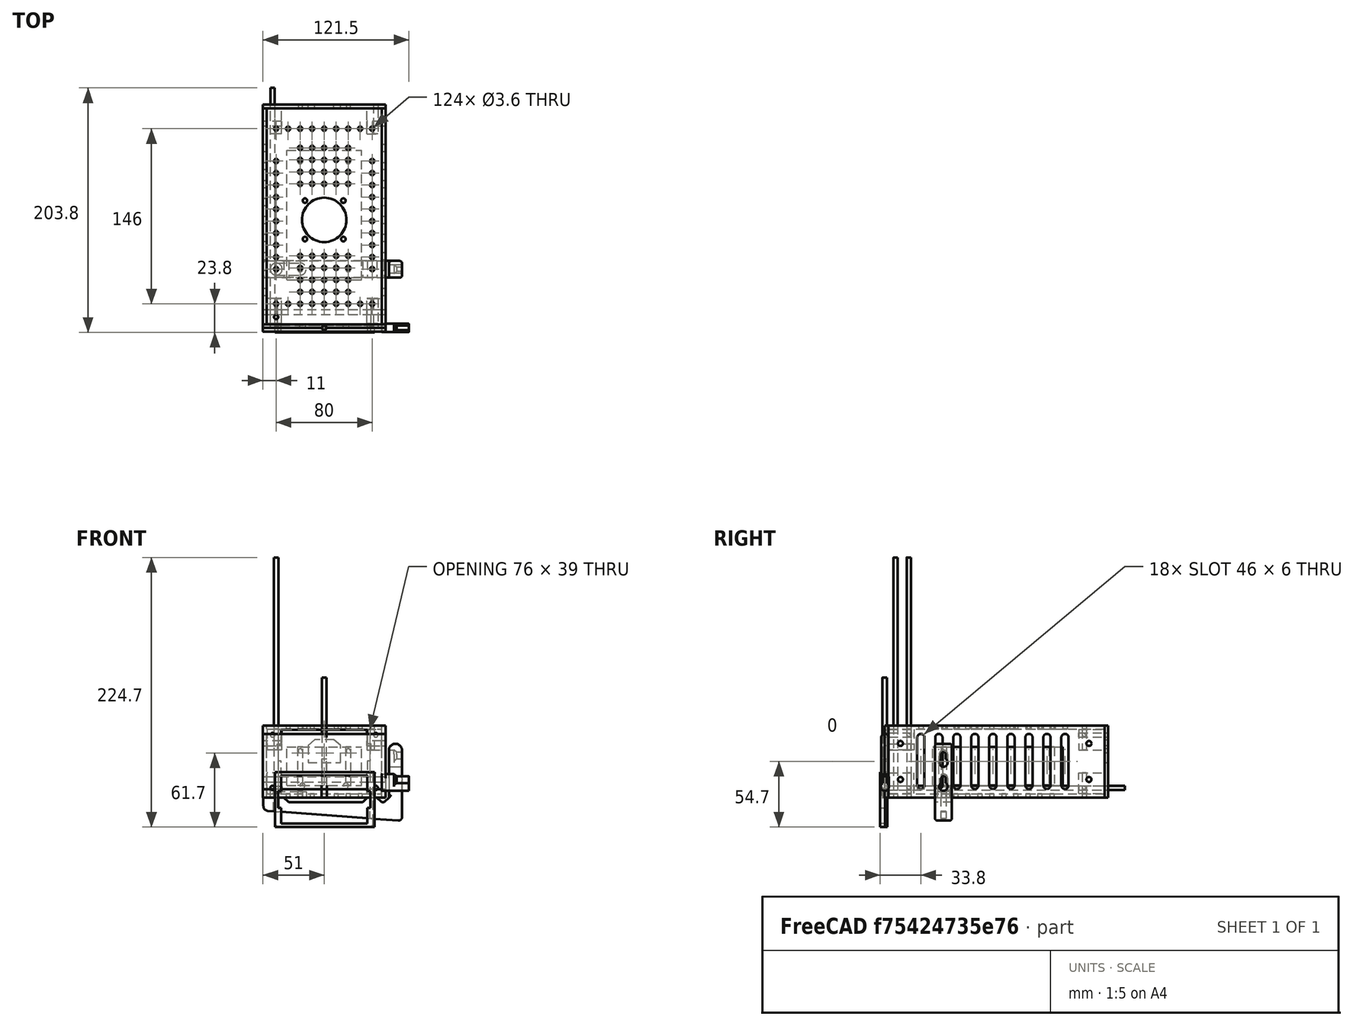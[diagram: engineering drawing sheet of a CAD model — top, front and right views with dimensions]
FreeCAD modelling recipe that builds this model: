
FCSTD DOCUMENT  (FreeCAD 0.21R33694 (Git))
Label: XY-SK35
License: All rights reserved
LicenseURL: http://en.wikipedia.org/wiki/All_rights_reserved
objects: Part::MultiFuse×13, Part::Box×12, Part::Cylinder×12, Part::Cut×10, Sketcher::SketchObject×9, Part::FeaturePython×9, Part::Extrusion×8, Part::Compound×3, Part::Mirroring×3, Part::Feature×1, Part::MultiCommon×1, Spreadsheet::Sheet×1, Part::Part2DObjectPython×1, Part::Fillet×1, Part::Loft×1
note: 75 computed .brp shape members not serialized (recipe doc carries the construction recipe); baked Part::Feature solids carry a one-line shape summary decoded from their .brp

FEATURE [Part::Box] Box  label="Cube"
  AttacherType = Attacher::AttachEngine3D
  Height = 32
  Length = 83
  Placement = pos=(8,29,0) rot=(0,0,1;0rad)
  Width = 46
FEATURE [Part::Feature] front_panel001001001_solid  label="front_panel001001001 (Solid)"
  shape: bbox 102 x 85 x 6 mm, 8704 faces (baked)
FEATURE [Part::MultiCommon] Common
  Placement = pos=(-49,-3.8,50.3) rot=(-1,0,0;1.5708rad)
  Shapes = -> [Box,front_panel001001001_solid]
FEATURE [Part::Box] Box001  label="display cube"
  AttacherType = Attacher::AttachEngine3D
  Height = 60
  Length = 102
  Placement = pos=(-51,0,0) rot=(0,0,1;0rad)
  Width = 3
  expr: .Placement.Base.x = -Length / 2
FEATURE [Part::Cylinder] Cylinder  label="hole_plus"
  Angle = 360
  AttacherType = Attacher::AttachEngine3D
  FirstAngle = 0
  Height = 10
  Placement = pos=(-18.1,10,10) rot=(1,0,0;1.5708rad)
  Radius = 2.1
  SecondAngle = 0
  expr: .Placement.Base.y = Height
FEATURE [Sketcher::SketchObject] Sketch  label="display hole sketch"
  FullyConstrained = true
  Placement = pos=(0,0,0) rot=(1,0,0;1.5708rad)
  sketch-geometry (12):
    g0: LineSegment StartX=-36 StartY=19.5 StartZ=0 EndX=36 EndY=19.5 EndZ=0
    g1: LineSegment StartX=36 StartY=19.5 StartZ=0 EndX=36 EndY=6.5 EndZ=0
    g2: LineSegment StartX=36 StartY=6.5 StartZ=0 EndX=38 EndY=6.5 EndZ=0
    g3: LineSegment StartX=38 StartY=6.5 StartZ=0 EndX=38 EndY=-6.5 EndZ=0
    g4: LineSegment StartX=38 StartY=-6.5 StartZ=0 EndX=36 EndY=-6.5 EndZ=0
    g5: LineSegment StartX=36 StartY=-6.5 StartZ=0 EndX=36 EndY=-19.5 EndZ=0
    g6: LineSegment StartX=36 StartY=-19.5 StartZ=0 EndX=-36 EndY=-19.5 EndZ=0
    g7: LineSegment StartX=-36 StartY=-19.5 StartZ=0 EndX=-36 EndY=-6.5 EndZ=0
    g8: LineSegment StartX=-36 StartY=-6.5 StartZ=0 EndX=-38 EndY=-6.5 EndZ=0
    g9: LineSegment StartX=-38 StartY=-6.5 StartZ=0 EndX=-38 EndY=6.5 EndZ=0
    g10: LineSegment StartX=-38 StartY=6.5 StartZ=0 EndX=-36 EndY=6.5 EndZ=0
    g11: LineSegment StartX=-36 StartY=6.5 StartZ=0 EndX=-36 EndY=19.5 EndZ=0
  constraints (36):
    c: Vertical(g1)
    c: Coincident(g2,g1)
    c: Horizontal(g2)
    c: Coincident(g3,g2)
    c: Coincident(g4,g3)
    c: Coincident(g5,g4)
    c: Vertical(g5)
    c: Coincident(g6,g5)
    c: Horizontal(g6)
    c: Coincident(g7,g6)
    c: Vertical(g7)
    c: Coincident(g8,g7)
    c: Coincident(g9,g8)
    c: Vertical(g9)
    c: Coincident(g10,g9)
    c: Horizontal(g10)
    c: Coincident(g11,g0)
    c: Vertical(g11)
    c: Equal(g0,g6)
    c: Equal(g7,g5)
    c: Equal(g3,g9)
    c: Equal(g10,g8)
    c: Equal(g8,g4)
    c: DistanceX(g0,g0) = 72
    c: DistanceY(g9,g9) = 13  'display_tab_height'
    c: Coincident(g11,g10)
    c: DistanceX(g10,g10) = 2
    c: Symmetric(g1,g10,g-2)
    c: Symmetric(g5,g0,g-1)
    c: Symmetric(g2,g3,g-1)
    c: DistanceY(g7,g7) = 13
    c: Coincident(g1,g0)
    c: Horizontal(g0)
    c: DistanceY(g5,g0) = 39  'display_hole_max_height'
    c: DistanceX(g9,g2) = 76  'display_hole_max_size'
    c: DistanceY(g5,g1) = 26  'bottom_to_tab_top'
FEATURE [Part::Extrusion] Extrude  label="display hole extrude"
  Base = -> Sketch
  Dir = (0,-1,2e-16)
  DirMode = 2
  FaceMakerClass = Part::FaceMakerBullseye
  LengthFwd = 10
  LengthRev = 0
  Placement = pos=(0,0,37) rot=(0,0,1;0rad)
  Reversed = true
  Solid = true
  Symmetric = false
FEATURE [Part::Cylinder] Cylinder001  label="hole_minus"
  Angle = 360
  AttacherType = Attacher::AttachEngine3D
  FirstAngle = 0
  Height = 10
  Placement = pos=(18.1,10,10) rot=(1,0,0;1.5708rad)
  Radius = 2.1
  SecondAngle = 0
  expr: .Placement.Base.x = -<<hole_plus>>.Placement.Base.x
  expr: .Placement.Base.y = <<hole_plus>>.Placement.Base.y
  expr: .Placement.Base.z = <<hole_plus>>.Placement.Base.z
  expr: Radius = <<hole_plus>>.Radius
FEATURE [Part::Cylinder] Cylinder002  label="bolt hole"
  Angle = 360
  AttacherType = Attacher::AttachEngine3D
  FirstAngle = 0
  Height = 200
  Placement = pos=(-43,200,8) rot=(1,0,0;1.5708rad)
  Radius = 1.8
  SecondAngle = 0
  expr: .Placement.Base.x = -<<display cube>>.Length / 2 + <<p>>.bolt2wall
  expr: .Placement.Base.y = Height
  expr: .Placement.Base.z = <<p>>.bolt2wall
  expr: Radius = <<p>>.bolt_hole_radius
FEATURE [Part::FeaturePython] Array  label="bolt hole array"  # Draft array (typed FeaturePython)
  AlwaysSyncPlacement = false
  Angle = 360
  ArrayType = 0
  Axis = (0,0,1)
  Base = -> Cylinder002
  Center = (0,0,0)
  Count = 4
  ExpandArray = false
  Fuse = false
  IntervalAxis = (0,0,0)
  IntervalX = (86,0,0)
  IntervalY = (0,100,0)
  IntervalZ = (0,0,44)
  NumberCircles = 3
  NumberPolar = 5
  NumberX = 2
  NumberY = 1
  NumberZ = 2
  PlacementList = 4 placements: [(-43,200,8),(-43,200,52),(43,200,8),(43,200,52)]
  RadialDistance = 50
  ScaleList = (4) [(1,1,1),(1,1,1),(1,1,1),(1,1,1)]
  Symmetry = 1
  TangentialDistance = 25
  expr: .IntervalX.x = <<display cube>>.Length - 2 * <<p>>.bolt2wall
  expr: .IntervalZ.z = <<display cube>>.Height - 2 * <<p>>.bolt2wall
FEATURE [Part::MultiFuse] Fusion  label="hole fusion"
  Shapes = -> [Array,Cylinder001,Cylinder,Extrude]
FEATURE [Part::Cut] Cut  label="front panel cut"
  Base = -> Box001
  Tool = -> Fusion
FEATURE [Spreadsheet::Sheet] Spreadsheet  label="p"
  cells = A1='bolt2wall; B1(bolt2wall)==8 mm; A2='plate_wall; B2(plate_wall)==3 mm; A3='bolt_hole_radius; B3(bolt_hole_radius)==1.8 mm; A4='fan_bolt_hole; B4(fan_bolt_hole)==2.2 mm; A5='fan_hole_radius; B5(fan_hole_radius)==18.5 mm; A6='screw_top_radius; B6(screw_top_radius)==3.5 mm; A7='screw_radius; B7(screw_radius)==1.8 mm
FEATURE [Part::Box] Box002  label="psu bottom cube"
  AttacherType = Attacher::AttachEngine3D
  Height = 3
  Length = 96
  Placement = pos=(-48,3,0) rot=(0,0,1;0rad)
  Width = 180
  expr: .Placement.Base.x = -Length / 2
  expr: .Placement.Base.y = <<p>>.plate_wall
  expr: Height = <<p>>.plate_wall
  expr: Length = <<display cube>>.Length - 2 * <<p>>.plate_wall
FEATURE [Part::Box] Box003  label="psu side cube"
  AttacherType = Attacher::AttachEngine3D
  Height = 60
  Length = 3
  Placement = pos=(-51,3,0) rot=(0,0,1;0rad)
  Width = 180
  expr: .Placement.Base.x = -<<display cube>>.Length / 2
  expr: .Placement.Base.y = <<p>>.plate_wall
  expr: Height = <<display cube>>.Height
  expr: Length = <<p>>.plate_wall
  expr: Width = <<psu bottom cube>>.Width
FEATURE [Part::Box] Box004  label="psu side cube001"
  AttacherType = Attacher::AttachEngine3D
  Height = 60
  Length = 3
  Placement = pos=(48,3,0) rot=(0,0,1;0rad)
  Width = 180
  expr: .Placement.Base.x = <<display cube>>.Length / 2 - <<p>>.plate_wall
  expr: .Placement.Base.y = <<p>>.plate_wall
  expr: Height = <<display cube>>.Height
  expr: Length = <<p>>.plate_wall
  expr: Width = <<psu bottom cube>>.Width
FEATURE [Part::Cylinder] Cylinder003  label="bolt side hole"
  Angle = 360
  AttacherType = Attacher::AttachEngine3D
  FirstAngle = 0
  Height = 102
  Placement = pos=(-51,13,15) rot=(0,1,0;1.5708rad)
  Radius = 2.1
  SecondAngle = 0
  expr: .Placement.Base.x = -<<display cube>>.Length / 2
  expr: .Placement.Base.y = <<p>>.plate_wall + 10 mm
  expr: Height = <<display cube>>.Length
FEATURE [Part::FeaturePython] Array001  label="bolt side hole array"  # Draft array (typed FeaturePython)
  AlwaysSyncPlacement = false
  Angle = 360
  ArrayType = 0
  Axis = (0,0,1)
  Base = -> Cylinder003
  Center = (0,0,0)
  Count = 4
  ExpandArray = false
  Fuse = false
  IntervalAxis = (0,0,0)
  IntervalX = (100,0,0)
  IntervalY = (0,157,0)
  IntervalZ = (0,0,30)
  NumberCircles = 3
  NumberPolar = 5
  NumberX = 1
  NumberY = 2
  NumberZ = 2
  PlacementList = 4 placements: [(-51,13,15),(-51,13,45),(-51,170,15),(-51,170,45)]
  RadialDistance = 50
  ScaleList = (4) [(1,1,1),(1,1,1),(1,1,1),(1,1,1)]
  Symmetry = 1
  TangentialDistance = 25
  expr: .IntervalY.y = <<psu bottom cube>>.Width - 2 * <<bolt side hole>>.Placement.Base.y + <<p>>.plate_wall
  expr: .IntervalZ.z = <<display cube>>.Height - 2 * <<bolt side hole>>.Placement.Base.z
FEATURE [Sketcher::SketchObject] Sketch001  label="side vent sketch"
  FullyConstrained = true
  Placement = pos=(0,0,0) rot=(0.57735,0.57735,0.57735;2.0944rad)
  expr: Constraints[9] = (<<psu side cube>>.Height - .Constraints.vent_hole_height) / 2
  sketch-geometry (4):
    g0: LineSegment StartX=-3 StartY=50 StartZ=0 EndX=-3 EndY=10 EndZ=0
    g1: LineSegment StartX=3 StartY=50 StartZ=0 EndX=3 EndY=10 EndZ=0
    g2: ArcOfCircle CenterX=0 CenterY=50 CenterZ=0 NormalX=0 NormalY=0 NormalZ=1 AngleXU=0 Radius=3 StartAngle=3e-16 EndAngle=3.14159
    g3: ArcOfCircle CenterX=1e-16 CenterY=10 CenterZ=0 NormalX=0 NormalY=0 NormalZ=1 AngleXU=0 Radius=3 StartAngle=3.14159 EndAngle=6.28319
  constraints (11):
    c: Vertical(g1)
    c: Vertical(g0)
    c: Coincident(g3,g1)
    c: Equal(g1,g0)
    c: Tangent(g2,g0) = -1.5708
    c: Tangent(g2,g1) = 1.5708
    c: Tangent(g3,g0) = -1.5708
    c: Radius(g3) = 3
    c: DistanceY(g0,g0) = 40  'vent_hole_height'
    c: DistanceY(g-1,g0) = 10
    c: PointOnObject(g2,g-2)
FEATURE [Part::Extrusion] Extrude001  label="side vent extrude"
  Base = -> Sketch001
  Dir = (1,0,0)
  DirMode = 2
  FaceMakerClass = Part::FaceMakerBullseye
  LengthFwd = 102
  LengthRev = 0
  Solid = true
  Symmetric = true
  expr: LengthFwd = <<display cube>>.Length
FEATURE [Part::FeaturePython] Array002  label="side vent array"  # Draft array (typed FeaturePython)
  AlwaysSyncPlacement = false
  Angle = 360
  ArrayType = 0
  Axis = (0,0,1)
  Base = -> Extrude001
  Center = (0,0,0)
  Count = 9
  ExpandArray = false
  Fuse = false
  IntervalAxis = (0,0,0)
  IntervalX = (100,0,0)
  IntervalY = (0,15,0)
  IntervalZ = (0,0,100)
  NumberCircles = 3
  NumberPolar = 5
  NumberX = 1
  NumberY = 9
  NumberZ = 1
  Placement = pos=(0,30,0) rot=(0,0,1;0rad)
  PlacementList = 9 placements: arithmetic series from (0,0,0) step (0,15,0) to (0,120,0)
  RadialDistance = 50
  ScaleList = (9) [(1,1,1),(1,1,1),(1,1,1),(1,1,1),(1,1,1),(1,1,1),(1,1,1),(1,1,1),(1,1,1)]
  Symmetry = 1
  TangentialDistance = 25
  expr: .IntervalY.y = (<<psu bottom cube>>.Width - .Placement.Base.y * 2) / (NumberY - 1)
FEATURE [Part::MultiFuse] Fusion001  label="side hole fusion"
  Shapes = -> [Array001,Array002]
FEATURE [Part::Cut] Cut001  label="psu side cut001"
  Base = -> Box004
  Tool = -> Fusion001
FEATURE [Part::Cut] Cut002  label="psu side cut"
  Base = -> Box003
  Tool = -> Fusion001
FEATURE [Part::Cylinder] Cylinder004  label="psu bottom bolt hole"
  Angle = 360
  AttacherType = Attacher::AttachEngine3D
  FirstAngle = 0
  Height = 200
  Placement = pos=(-40,20,0) rot=(0,0,1;0rad)
  Radius = 1.8
  SecondAngle = 0
  expr: .Placement.Base.x = -<<display cube>>.Length / 2 + <<p>>.bolt2wall + <<p>>.plate_wall
  expr: Radius = <<p>>.bolt_hole_radius
FEATURE [Part::FeaturePython] Array003  label="psu bottom bolt hole array"  # Draft array (typed FeaturePython)
  AlwaysSyncPlacement = false
  Angle = 360
  ArrayType = 0
  Axis = (0,0,1)
  Base = -> Cylinder004
  Center = (0,0,0)
  Count = 18
  ExpandArray = false
  Fuse = false
  IntervalAxis = (0,0,0)
  IntervalX = (10,0,0)
  IntervalY = (0,146,0)
  IntervalZ = (0,0,100)
  NumberCircles = 3
  NumberPolar = 5
  NumberX = 9
  NumberY = 2
  NumberZ = 1
  PlacementList = 18 placements: [(-40,20,0),(-40,166,0),(-30,20,0),(-30,166,0),(-20,20,0),(-20,166,0),(-10,20,0),(-10,166,0),(0,20,0),(0,166,0),(10,20,0),(10,166,0),(20,20,0),(20,166,0),(30,20,0),(30,166,0),(40,20,0),(40,166,0)]
  RadialDistance = 50
  ScaleList = (18) [(1,1,1),(1,1,1),(1,1,1),(1,1,1),(1,1,1),(1,1,1),(1,1,1),(1,1,1),(1,1,1),(1,1,1),(1,1,1),(1,1,1),(1,1,1),(1,1,1),(1,1,1),(1,1,1),(1,1,1),(1,1,1)]
  Symmetry = 1
  TangentialDistance = 25
  expr: .IntervalX.x = abs(<<psu bottom bolt hole>>.Placement.Base.x) * 2 / (NumberX - 1)
  expr: .IntervalY.y = <<psu bottom cube>>.Width - <<psu bottom bolt hole>>.Placement.Base.y * 2 + 2 * <<p>>.plate_wall
FEATURE [Part::Cylinder] Cylinder005  label="psu mockup hole"
  Angle = 360
  AttacherType = Attacher::AttachEngine3D
  FirstAngle = 0
  Height = 32
  Radius = 2.2
  SecondAngle = 0
  expr: Height = <<psu mockup>>.Height
FEATURE [Part::FeaturePython] Array004  label="psu mockup hole array"  # Draft array (typed FeaturePython)
  AlwaysSyncPlacement = false
  Angle = 360
  ArrayType = 0
  Axis = (0,0,1)
  Base = -> Cylinder005
  Center = (0,0,0)
  Count = 4
  ExpandArray = false
  Fuse = false
  IntervalAxis = (0,0,0)
  IntervalX = (40,0,0)
  IntervalY = (0,90,0)
  IntervalZ = (0,0,100)
  NumberCircles = 3
  NumberPolar = 5
  NumberX = 2
  NumberY = 2
  NumberZ = 1
  Placement = pos=(11,9,0) rot=(0,0,1;0rad)
  PlacementList = 4 placements: [(0,0,0),(0,90,0),(40,0,0),(40,90,0)]
  RadialDistance = 50
  ScaleList = (4) [(1,1,1),(1,1,1),(1,1,1),(1,1,1)]
  Symmetry = 1
  TangentialDistance = 25
  expr: .Placement.Base.x = (<<psu mockup>>.Length - .IntervalX.x) / 2
  expr: .Placement.Base.y = (<<psu mockup>>.Width - .IntervalY.y) / 2
FEATURE [Part::Box] Box005  label="psu mockup"
  AttacherType = Attacher::AttachEngine3D
  Height = 32
  Length = 62
  Width = 108
FEATURE [Part::Cut] Cut003  label="psu mockup with holes"
  Base = -> Box005
  Placement = pos=(-31,40,10) rot=(0,0,1;0rad)
  Tool = -> Array004
  expr: .Placement.Base.x = -<<psu mockup>>.Length / 2
FEATURE [Part::Cylinder] Cylinder006  label="psu bottom holder hole"
  Angle = 360
  AttacherType = Attacher::AttachEngine3D
  FirstAngle = 0
  Height = 200
  Placement = pos=(-40,9,0) rot=(0,0,1;0rad)
  Radius = 1.8
  SecondAngle = 0
  expr: .Placement.Base.x = -<<display cube>>.Length / 2 + <<p>>.bolt2wall + <<p>>.plate_wall
  expr: .Placement.Base.y = abs(<<psu mockup>>.Placement.Base.y + <<psu mockup hole array>>.Placement.Base.y)
  expr: Radius = <<p>>.bolt_hole_radius
FEATURE [Part::FeaturePython] Array005  label="psu bottom holder bolt hole array"  # Draft array (typed FeaturePython)
  AlwaysSyncPlacement = false
  Angle = 360
  ArrayType = 0
  Axis = (0,0,1)
  Base = -> Cylinder006
  Center = (0,0,0)
  Count = 20
  ExpandArray = false
  Fuse = false
  IntervalAxis = (0,0,0)
  IntervalX = (80,0,0)
  IntervalY = (0,10,0)
  IntervalZ = (0,0,100)
  NumberCircles = 3
  NumberPolar = 5
  NumberX = 2
  NumberY = 10
  NumberZ = 1
  Placement = pos=(0,40,0) rot=(0,0,1;0rad)
  PlacementList = 20 placements: [(-40,9,0),(-40,19,0),(-40,29,0),(-40,39,0),(-40,49,0),(-40,59,0),(-40,69,0),(-40,79,0),(-40,89,0),(-40,99,0),(40,9,0),(40,19,0),(40,29,0),(40,39,0),(40,49,0),(40,59,0),(40,69,0),(40,79,0),(40,89,0),(40,99,0)]
  RadialDistance = 50
  ScaleList = (20) [(1,1,1),(1,1,1),(1,1,1),(1,1,1),(1,1,1),(1,1,1),(1,1,1),(1,1,1),(1,1,1),(1,1,1),(1,1,1),(1,1,1),(1,1,1),(1,1,1),(1,1,1),(1,1,1),(1,1,1),(1,1,1),+2 more]
  Symmetry = 1
  TangentialDistance = 25
  expr: .IntervalX.x = abs(<<psu bottom holder hole>>.Placement.Base.x) * 2 / (NumberX - 1)
  expr: .IntervalY.y = <<psu mockup hole array>>.IntervalY.y / (NumberY - 1)
  expr: .Placement.Base.y = <<psu mockup with holes>>.Placement.Base.y
FEATURE [Part::MultiFuse] Fusion002  label="bottom hole fusion"
  Shapes = -> [Array005,Array003]
FEATURE [Part::Cut] Cut004  label="psu bottom cut"
  Base = -> Box002
  Tool = -> Fusion002
FEATURE [Part::Part2DObjectPython] Shape2DView  # Draft 2D object (typed FeaturePython)
  AutoUpdate = true
  Base = -> Cut
  Clip = false
  FaceNumbers = [1]
  FuseArch = false
  HiddenLines = false
  InPlace = true
  OnlySolids = false
  Projection = (0,-1,0)
  ProjectionMode = 0
  SegmentLength = 0.05
  Tessellation = false
  VisibleOnly = false
FEATURE [Sketcher::SketchObject] Sketch002
  FullyConstrained = false
  sketch-geometry (22):
    g0: LineSegment StartX=0 StartY=-51 StartZ=0 EndX=-60 EndY=-51 EndZ=0
    g1: LineSegment StartX=0 StartY=-51 StartZ=0 EndX=0 EndY=51 EndZ=0
    g2: LineSegment StartX=0 StartY=51 StartZ=0 EndX=-60 EndY=51 EndZ=0
    g3: LineSegment StartX=-60 StartY=-51 StartZ=0 EndX=-60 EndY=51 EndZ=0
    g4: Circle CenterX=-8 CenterY=-43 CenterZ=0 NormalX=0 NormalY=0 NormalZ=1 AngleXU=1.5708 Radius=1.8
    g5: Circle CenterX=-10 CenterY=-18.1 CenterZ=0 NormalX=0 NormalY=0 NormalZ=1 AngleXU=1.5708 Radius=2.1
    g6: Circle CenterX=-52 CenterY=-43 CenterZ=0 NormalX=0 NormalY=0 NormalZ=1 AngleXU=1.5708 Radius=1.8
    g7: Circle CenterX=-10 CenterY=18.1 CenterZ=0 NormalX=0 NormalY=0 NormalZ=1 AngleXU=1.5708 Radius=2.1
    g8: Circle CenterX=-8 CenterY=43 CenterZ=0 NormalX=0 NormalY=0 NormalZ=1 AngleXU=1.5708 Radius=1.8
    g9: LineSegment StartX=-56.5 StartY=-36 StartZ=0 EndX=-56.5 EndY=36 EndZ=0
    g10: LineSegment StartX=-56.5 StartY=36 StartZ=0 EndX=-43.5 EndY=36 EndZ=0
    g11: LineSegment StartX=-43.5 StartY=36 StartZ=0 EndX=-43.5 EndY=38 EndZ=0
    g12: LineSegment StartX=-43.5 StartY=38 StartZ=0 EndX=-30.5 EndY=38 EndZ=0
    g13: LineSegment StartX=-30.5 StartY=38 StartZ=0 EndX=-30.5 EndY=36 EndZ=0
    g14: LineSegment StartX=-30.5 StartY=36 StartZ=0 EndX=-17.5 EndY=36 EndZ=0
    g15: LineSegment StartX=-17.5 StartY=36 StartZ=0 EndX=-17.5 EndY=-36 EndZ=0
    g16: LineSegment StartX=-17.5 StartY=-36 StartZ=0 EndX=-30.5 EndY=-36 EndZ=0
    g17: LineSegment StartX=-30.5 StartY=-36 StartZ=0 EndX=-30.5 EndY=-38 EndZ=0
    g18: LineSegment StartX=-30.5 StartY=-38 StartZ=0 EndX=-43.5 EndY=-38 EndZ=0
    g19: LineSegment StartX=-43.5 StartY=-38 StartZ=0 EndX=-43.5 EndY=-36 EndZ=0
    g20: LineSegment StartX=-43.5 StartY=-36 StartZ=0 EndX=-56.5 EndY=-36 EndZ=0
    g21: Circle CenterX=-52 CenterY=43 CenterZ=0 NormalX=0 NormalY=0 NormalZ=1 AngleXU=1.5708 Radius=1.8
FEATURE [Part::Box] Box006  label="bolt cube"
  AttacherType = Attacher::AttachEngine3D
  Height = 17
  Length = 12
  Placement = pos=(35.6,3.4,3.4) rot=(0,0,1;0rad)
  Width = 21
  expr: .Placement.Base.x = <<display cube>>.Length / 2 - Length - (<<p>>.plate_wall + 0.4 mm)
  expr: .Placement.Base.y = <<p>>.plate_wall + 0.4 mm
  expr: .Placement.Base.z = <<p>>.plate_wall + 0.4 mm
FEATURE [Part::MultiFuse] Fusion003  label="all bolt hole array"
  Shapes = -> [Array,Array001,Fusion002]
FEATURE [Part::Box] Box007  label="bolt cube001"
  AttacherType = Attacher::AttachEngine3D
  Height = 17
  Length = 12
  Placement = pos=(35.6,161.6,3.4) rot=(0,0,1;0rad)
  Width = 21
  expr: .Placement.Base.x = <<display cube>>.Length / 2 - Length - (<<p>>.plate_wall + 0.4 mm)
  expr: .Placement.Base.y = -Width - 0.4 mm + <<p>>.plate_wall + <<psu bottom cube>>.Width
  expr: .Placement.Base.z = <<p>>.plate_wall + 0.4 mm
FEATURE [Part::Compound] Compound  label="bolt cube compound"
  Links = -> [Box006,Box007]
FEATURE [Part::Mirroring] Part__Mirroring002  label="bolt cube compound (Mirror #3)"
  Base = (0,0,0)
  Normal = (1,0,0)
  Source = -> Compound
FEATURE [Part::MultiFuse] Fusion004  label="bolt cube fusion"
  Shapes = -> [Part__Mirroring002,Compound]
FEATURE [Part::Mirroring] Part__Mirroring003  label="bolt cube fusion (Mirror #4)"
  Base = (0,0,30)
  Normal = (0,0,1)
  Source = -> Fusion004
  expr: .Base.z = <<display cube>>.Height / 2
FEATURE [Part::MultiFuse] Fusion005  label="bolt cube full fusion"
  Shapes = -> [Part__Mirroring003,Fusion004]
FEATURE [Part::Box] Box008  label="back cube"
  AttacherType = Attacher::AttachEngine3D
  Height = 60
  Length = 102
  Placement = pos=(-51,183,0) rot=(0,0,1;0rad)
  Width = 3
  expr: .Placement.Base.x = -Length / 2
  expr: .Placement.Base.y = <<psu bottom cube>>.Width + <<p>>.plate_wall
  expr: Height = <<display cube>>.Height
  expr: Length = <<display cube>>.Length
  expr: Width = <<p>>.plate_wall
FEATURE [Sketcher::SketchObject] Sketch003  label="power input sketch"
  FullyConstrained = false
  expr: Constraints[19] = .Constraints.height / 2
  expr: Constraints[20] = .Constraints.height / 2
  expr: Constraints[23] = (.Constraints.hole_dist - .Constraints.bottom_size) / 2
  expr: Constraints[9] = (.Constraints.bottom_size - .Constraints.top_size) / 2
  sketch-geometry (8):
    g0: LineSegment StartX=45.61 StartY=11.9107 StartZ=0 EndX=45.61 EndY=25.9107 EndZ=0
    g1: LineSegment StartX=45.61 StartY=25.9107 StartZ=0 EndX=51.11 EndY=30.9107 EndZ=0
    g2: LineSegment StartX=51.11 StartY=30.9107 StartZ=0 EndX=67.11 EndY=30.9107 EndZ=0
    g3: LineSegment StartX=67.11 StartY=30.9107 StartZ=0 EndX=72.61 EndY=25.9107 EndZ=0
    g4: LineSegment StartX=72.61 StartY=25.9107 StartZ=0 EndX=72.61 EndY=11.9107 EndZ=0
    g5: LineSegment StartX=72.61 StartY=11.9107 StartZ=0 EndX=45.61 EndY=11.9107 EndZ=0
    g6: Circle CenterX=39.11 CenterY=21.4107 CenterZ=0 NormalX=0 NormalY=0 NormalZ=1 AngleXU=0 Radius=1.8
    g7: Circle CenterX=79.11 CenterY=21.4107 CenterZ=0 NormalX=0 NormalY=0 NormalZ=1 AngleXU=0 Radius=1.8
  constraints (24):
    c: Horizontal(g5)
    c: Vertical(g4)
    c: Horizontal(g2)
    c: Vertical(g0)
    c: DistanceX(g2,g2) = 16  'top_size'
    c: DistanceY(g5,g2) = 19  'height'
    c: DistanceX(g5,g5) = 27  'bottom_size'
    c: DistanceY(g4,g4) = 14
    c: Equal(g4,g0)
    c: DistanceX(g5,g2) = 5.5
    c: Coincident(g4,g5)
    c: Coincident(g0,g5)
    c: Coincident(g0,g1)
    c: Coincident(g3,g4)
    c: Coincident(g1,g2)
    c: Coincident(g3,g2)
    c: Radius(g6) = 1.8
    c: Equal(g6,g7)
    c: DistanceY(g0,g0) = 14  'side_size'
    c: DistanceY(g0,g6) = 9.5
    c: DistanceY(g4,g7) = 9.5
    c: DistanceY(g7,g2) = 9.5
    c: DistanceX(g6,g7) = 40  'hole_dist'
    c: DistanceX(g6,g0) = 6.5
FEATURE [Part::Extrusion] Extrude002  label="power input extrude"
  Base = -> Sketch003
  Dir = (0,0,1)
  DirMode = 2
  FaceMakerClass = Part::FaceMakerBullseye
  LengthFwd = 10
  LengthRev = 0
  Placement = pos=(-59,180,17.3) rot=(1,0,0;1.5708rad)
  Reversed = true
  Solid = true
  Symmetric = false
  expr: .Placement.Base.y = <<psu bottom cube>>.Width
FEATURE [Part::MultiFuse] Fusion006  label="back wall hole fusion"
  Shapes = -> [Array,Extrude002]
FEATURE [Part::Cut] Cut009  label="back wall cut"
  Base = -> Box008
  Tool = -> Fusion006
FEATURE [Part::Box] Box009  label="psu top cube"
  AttacherType = Attacher::AttachEngine3D
  Height = 3
  Length = 96
  Placement = pos=(-48,3,57) rot=(0,0,1;0rad)
  Width = 180
  expr: .Placement.Base.x = -Length / 2
  expr: .Placement.Base.y = <<p>>.plate_wall
  expr: .Placement.Base.z = <<display cube>>.Height - <<p>>.plate_wall
  expr: Height = <<p>>.plate_wall
  expr: Length = <<display cube>>.Length - 2 * <<p>>.plate_wall
FEATURE [Part::Box] Box010  label="display max hole size cube"
  AttacherType = Attacher::AttachEngine3D
  Height = 13
  Length = 78
  Placement = pos=(-39,0,31.5) rot=(0,0,1;0rad)
  Width = 30
  expr: .Placement.Base.x = -Length / 2
  expr: .Placement.Base.z = <<display hole extrude>>.Placement.Base.z - <<display hole sketch>>.Constraints.display_hole_max_height / 2 + <<display hole sketch>>.Constraints.bottom_to_tab_top - Height + 1 mm
  expr: Height = <<display hole sketch>>.Constraints.display_tab_height
  expr: Length = <<display hole sketch>>.Constraints.display_hole_max_size + 2 mm
FEATURE [Part::MultiFuse] Fusion007  label="all hole fusion"
  Shapes = -> [Fusion003,Box010]
FEATURE [Part::Cut] Cut008  label="bolt cube full cut"
  Base = -> Fusion005
  Tool = -> Fusion007
FEATURE [Sketcher::SketchObject] Sketch004  label="psu two hole tab"
  FullyConstrained = false
  sketch-geometry (6):
    g0: LineSegment StartX=-39.9637 StartY=54.0177 StartZ=0 EndX=-19.9637 EndY=54.0177 EndZ=0
    g1: LineSegment StartX=-39.9637 StartY=44.0177 StartZ=0 EndX=-19.9637 EndY=44.0177 EndZ=0
    g2: ArcOfCircle CenterX=-39.9637 CenterY=49.0177 CenterZ=0 NormalX=0 NormalY=0 NormalZ=1 AngleXU=0 Radius=5 StartAngle=1.5708 EndAngle=4.71239
    g3: ArcOfCircle CenterX=-19.9637 CenterY=49.0177 CenterZ=0 NormalX=0 NormalY=0 NormalZ=1 AngleXU=0 Radius=5 StartAngle=4.71239 EndAngle=7.85398
    g4: Circle CenterX=-39.9637 CenterY=49.0177 CenterZ=0 NormalX=0 NormalY=0 NormalZ=1 AngleXU=0 Radius=2.2
    g5: Circle CenterX=-19.9637 CenterY=49.0177 CenterZ=0 NormalX=0 NormalY=0 NormalZ=1 AngleXU=0 Radius=2.2
  constraints (12):
    c: Horizontal(g0)
    c: Horizontal(g1)
    c: Tangent(g2,g0) = 1.5708
    c: Tangent(g2,g1) = -1.5708
    c: Tangent(g3,g1) = -1.5708
    c: Tangent(g3,g0) = 1.5708
    c: Coincident(g4,g2)
    c: Coincident(g5,g3)
    c: Radius(g5) = 2.2
    c: Equal(g5,g4)
    c: DistanceY(g3,g0) = 5
    c: DistanceX(g2,g3) = 20
FEATURE [Part::Extrusion] Extrude003  label="psu two hole tab extrude"
  Base = -> Sketch004
  Dir = (0,0,1)
  DirMode = 2
  FaceMakerClass = Part::FaceMakerBullseye
  LengthFwd = 5
  LengthRev = 0
  Solid = true
  Symmetric = false
FEATURE [Sketcher::SketchObject] Sketch005  label="psu one hole"
  ExternalGeometry = -> [Extrude003]
  FullyConstrained = false
  sketch-geometry (2):
    g0: Circle CenterX=-39.9637 CenterY=49.0177 CenterZ=0 NormalX=0 NormalY=0 NormalZ=1 AngleXU=0 Radius=5
    g1: Circle CenterX=-39.9591 CenterY=49.0206 CenterZ=0 NormalX=0 NormalY=0 NormalZ=1 AngleXU=0 Radius=2.10546
  constraints (2):
    c: Coincident(g0,g-3)
    c: PointOnObject(g-3,g0)
FEATURE [Part::Extrusion] Extrude004  label="psu one hole extrude"
  Base = -> Sketch005
  Dir = (0,0,1)
  DirMode = 2
  FaceMakerClass = Part::FaceMakerBullseye
  LengthFwd = 9
  LengthRev = 0
  Solid = true
  Symmetric = false
  expr: LengthFwd = <<psu two hole tab extrude>>.LengthFwd + 4 mm
FEATURE [Part::MultiFuse] Fusion008  label="psu two hole tab fusion"
  Shapes = -> [Extrude003,Extrude004]
FEATURE [Sketcher::SketchObject] Sketch006  label="hand sketch"
  FullyConstrained = false
  Placement = pos=(0,0,0) rot=(1,0,0;1.5708rad)
  sketch-geometry (15):
    g0: LineSegment StartX=-50.6262 StartY=0 StartZ=0 EndX=-50.6262 EndY=-7.18825 EndZ=0
    g1: LineSegment StartX=-46.9029 StartY=-11.1988 StartZ=0 EndX=61.6639 EndY=-19.2736 EndZ=0
    g2: LineSegment StartX=64.8509 StartY=-16.3148 StartZ=0 EndX=64.8509 EndY=39.2594 EndZ=0
    g3: LineSegment StartX=53.8509 StartY=39.2594 StartZ=0 EndX=53.8509 EndY=0 EndZ=0
    g4: LineSegment StartX=43.9997 StartY=0 StartZ=0 EndX=35.9997 EndY=0 EndZ=0
    g5: LineSegment StartX=35.9997 StartY=0 StartZ=0 EndX=31.9997 EndY=-4 EndZ=0
    g6: LineSegment StartX=31.9997 StartY=-4 StartZ=0 EndX=-29.6262 EndY=-4 EndZ=0
    g7: LineSegment StartX=-29.6262 StartY=-4 StartZ=0 EndX=-33.6262 EndY=0 EndZ=0
    g8: LineSegment StartX=-33.6262 StartY=0 StartZ=0 EndX=-50.6262 EndY=0 EndZ=0
    g9: ArcOfCircle CenterX=59.3509 CenterY=39.2594 CenterZ=0 NormalX=0 NormalY=0 NormalZ=1 AngleXU=0 Radius=5.5 StartAngle=0 EndAngle=3.14159
    g10: ArcOfCircle CenterX=-46.6046 CenterY=-7.18825 CenterZ=0 NormalX=0 NormalY=0 NormalZ=1 AngleXU=0 Radius=4.02167 StartAngle=3.14159 EndAngle=4.63815
    g11: ArcOfCircle CenterX=61.8839 CenterY=-16.3148 CenterZ=0 NormalX=0 NormalY=0 NormalZ=1 AngleXU=0 Radius=2.96695 StartAngle=4.63815 EndAngle=6.28319
    g12: LineSegment StartX=43.9997 StartY=0 StartZ=0 EndX=47.9997 EndY=-4 EndZ=0
    g13: LineSegment StartX=47.9997 StartY=-4 StartZ=0 EndX=49.8509 EndY=-4 EndZ=0
    g14: LineSegment StartX=49.8509 StartY=-4 StartZ=0 EndX=53.8509 EndY=0 EndZ=0
  constraints (34):
    c: Vertical(g2)
    c: PointOnObject(g3,g-1)
    c: Vertical(g3)
    c: PointOnObject(g4,g-1)
    c: Horizontal(g6)
    c: PointOnObject(g7,g-1)
    c: Coincident(g8,g7)
    c: Tangent(g9,g2) = -1.5708
    c: Tangent(g9,g3) = -1.5708
    c: DistanceX(g3,g2) = 11
    c: Coincident(g5,g4)
    c: Coincident(g6,g5)
    c: Angle(g5,g6) = 2.35619
    c: Coincident(g6,g7)
    c: Angle(g6,g7) = 2.35619
    c: Tangent(g1,g10) = -1.5708
    c: Tangent(g0,g10) = -1.5708
    c: Tangent(g1,g11) = -1.5708
    c: Tangent(g2,g11) = -1.5708
    c: DistanceY(g6,g-1) = 4
    c: Coincident(g8,g0)
    c: DistanceX(g8,g8) = 17
    c: DistanceX(g4,g4) = 8
    c: Coincident(g12,g4)
    c: Coincident(g13,g12)
    c: Coincident(g14,g13)
    c: Coincident(g14,g3)
    c: Horizontal(g13)
    c: DistanceY(g13,g-1) = 4
    c: Angle(g13,g12) = 2.35619
    c: Angle(g14,g13) = 2.35619
    c: Horizontal(g4)
    c: Vertical(g0)
    c: Horizontal(g8)
FEATURE [Part::Extrusion] Extrude005  label="hand extrude"
  Base = -> Sketch006
  Dir = (0,-1,2e-16)
  DirMode = 2
  FaceMakerClass = Part::FaceMakerBullseye
  LengthFwd = 14
  LengthRev = 0
  Solid = true
  Symmetric = true
FEATURE [Part::Cylinder] Cylinder007  label="bolt hole001"
  Angle = 360
  AttacherType = Attacher::AttachEngine3D
  FirstAngle = 0
  Height = 50
  Placement = pos=(40,0,-50) rot=(0,0,1;0rad)
  Radius = 2.2
  SecondAngle = 0
  expr: .Placement.Base.z = -Height
FEATURE [Part::Mirroring] Part__Mirroring  label="bolt hole001 (Mirror #3)"
  Base = (0,0,0)
  Normal = (1,0,0)
  Source = -> Cylinder007
FEATURE [Part::Fillet] Fillet  label="hand fillet"
  Base = -> Extrude005
  Edges = 2 edges r=2: [Edge24,Edge25]
FEATURE [Part::Cylinder] Cylinder009  label="screw top hole"
  Angle = 360
  AttacherType = Attacher::AttachEngine3D
  FirstAngle = 0
  Height = 12.5
  Placement = pos=(7,0,0) rot=(0,0,1;0rad)
  Radius = 3.5
  SecondAngle = 0
  expr: .Placement.Base.x = <<p>>.screw_top_radius * 2
  expr: Radius = <<p>>.screw_top_radius
FEATURE [Part::Cylinder] Cylinder010  label="fan bolt hole"
  Angle = 360
  AttacherType = Attacher::AttachEngine3D
  FirstAngle = 0
  Height = 100
  Radius = 1.9
  SecondAngle = 0
  expr: Height = <<fan hole>>.Height
FEATURE [Part::FeaturePython] Array007  label="fan bolt hole array"  # Draft array (typed FeaturePython)
  AlwaysSyncPlacement = false
  Angle = 360
  ArrayType = 0
  Axis = (0,0,1)
  Base = -> Cylinder010
  Center = (0,0,0)
  Count = 4
  ExpandArray = false
  Fuse = false
  IntervalAxis = (0,0,0)
  IntervalX = (32,0,0)
  IntervalY = (0,32,0)
  IntervalZ = (0,0,100)
  NumberCircles = 3
  NumberPolar = 5
  NumberX = 2
  NumberY = 2
  NumberZ = 1
  Placement = pos=(-16,-16,0) rot=(0,0,1;0rad)
  PlacementList = 4 placements: [(0,0,0),(0,32,0),(32,0,0),(32,32,0)]
  RadialDistance = 50
  ScaleList = (4) [(1,1,1),(1,1,1),(1,1,1),(1,1,1)]
  Symmetry = 1
  TangentialDistance = 25
FEATURE [Part::Cylinder] Cylinder011  label="fan hole"
  Angle = 360
  AttacherType = Attacher::AttachEngine3D
  FirstAngle = 0
  Height = 100
  Radius = 18.5
  SecondAngle = 0
  expr: Radius = <<p>>.fan_hole_radius
FEATURE [Part::MultiFuse] Fusion011  label="fan hole fusion"
  Placement = pos=(0,90,0) rot=(0,0,1;0rad)
  Shapes = -> [Array007,Cylinder011]
  expr: .Placement.Base.y = <<psu top cube>>.Width / 2
FEATURE [Part::Cylinder] Cylinder012  label="top ventilation hole"
  Angle = 360
  AttacherType = Attacher::AttachEngine3D
  FirstAngle = 0
  Height = 100
  Radius = 1.8
  SecondAngle = 0
  expr: Radius = <<p>>.bolt_hole_radius
FEATURE [Part::FeaturePython] Array008  label="top ventilation array"  # Draft array (typed FeaturePython)
  AlwaysSyncPlacement = false
  Angle = 360
  ArrayType = 0
  Axis = (0,0,1)
  Base = -> Cylinder012
  Center = (0,0,0)
  Count = 65
  ExpandArray = false
  Fuse = false
  IntervalAxis = (0,0,0)
  IntervalX = (10,0,0)
  IntervalY = (0,10,0)
  IntervalZ = (0,0,100)
  NumberCircles = 3
  NumberPolar = 5
  NumberX = 5
  NumberY = 13
  NumberZ = 1
  Placement = pos=(-20,30,0) rot=(0,0,1;0rad)
  PlacementList = 65 placements: [(0,0,0),(0,10,0),(0,20,0),(0,30,0),(0,40,0),(0,50,0),(0,60,0),(0,70,0),(0,80,0),(0,90,0),(0,100,0),(0,110,0),(0,120,0),(10,0,0),(10,10,0),(10,20,0),(10,30,0),(10,40,0),(10,50,0),(10,60,0),(10,70,0),(10,80,0),(10,90,0),(10,100,0),(10,110,0),(10,120,0),(20,0,0),(20,10,0),(20,20,0),(20,30,0),(20,40,0),(20,50,0),(20,60,0),(20,70,0),(20,80,0),(20,90,0),(20,100,0),(20,110,0),(20,120,0),(30,0,0),+25 more]
  RadialDistance = 50
  ScaleList = (65) [(1,1,1),(1,1,1),(1,1,1),(1,1,1),(1,1,1),(1,1,1),(1,1,1),(1,1,1),(1,1,1),(1,1,1),(1,1,1),(1,1,1),(1,1,1),(1,1,1),(1,1,1),(1,1,1),(1,1,1),(1,1,1),+47 more]
  Symmetry = 1
  TangentialDistance = 25
  expr: .Placement.Base.x = -(.IntervalX.x * (NumberX - 1)) / 2
FEATURE [Part::Box] Box011  label="no vent hole cube"
  AttacherType = Attacher::AttachEngine3D
  Height = 100
  Length = 50
  Placement = pos=(-25,66,0) rot=(0,0,1;0rad)
  Width = 50
  expr: .Placement.Base.x = -Length / 2
FEATURE [Part::Cut] Cut012  label="vent holes cut"
  Base = -> Array008
  Tool = -> Box011
FEATURE [Part::MultiFuse] Fusion012  label="top hole fusion"
  Shapes = -> [Array005,Array003,Cut012,Fusion011]
FEATURE [Part::Cut] Cut010  label="psu top cut"
  Base = -> Box009
  Tool = -> Fusion012
FEATURE [Part::Compound] Compound001  label="box compound"
  Links = -> [Cut009,Cut008,Cut004,Cut001,Cut002,Cut,Cut010]
FEATURE [Sketcher::SketchObject] Sketch007  label="screw top hole sketch"
  FullyConstrained = true
  expr: Constraints[7] = <<p>>.screw_top_radius
  expr: Constraints[8] = <<p>>.screw_top_radius * 2
  sketch-geometry (4):
    g0: LineSegment StartX=-3e-16 StartY=3.5 StartZ=0 EndX=7 EndY=3.5 EndZ=0
    g1: LineSegment StartX=4e-16 StartY=-3.5 StartZ=0 EndX=7 EndY=-3.5 EndZ=0
    g2: ArcOfCircle CenterX=3.83e-14 CenterY=0 CenterZ=0 NormalX=0 NormalY=0 NormalZ=1 AngleXU=0 Radius=3.5 StartAngle=1.5708 EndAngle=4.71239
    g3: ArcOfCircle CenterX=7 CenterY=-1.007e-13 CenterZ=0 NormalX=0 NormalY=0 NormalZ=1 AngleXU=0 Radius=3.5 StartAngle=4.71239 EndAngle=7.85398
  constraints (9):
    c: PointOnObject(g0,g-2)
    c: Horizontal(g0)
    c: Tangent(g3,g1) = -1.5708
    c: Tangent(g3,g0) = 1.5708
    c: Tangent(g2,g1) = -1.5708
    c: Tangent(g2,g0) = 1.5708
    c: Symmetric(g1,g0,g-1)
    c: Radius(g2) = 3.5
    c: DistanceX(g2,g3) = 7
FEATURE [Sketcher::SketchObject] Sketch008  label="screw hole sketch"
  FullyConstrained = true
  Placement = pos=(0,0,2.5) rot=(0,0,1;0rad)
  expr: Constraints[7] = <<p>>.screw_radius
  expr: Constraints[8] = <<p>>.screw_top_radius * 2
  sketch-geometry (4):
    g0: LineSegment StartX=0 StartY=1.8 StartZ=0 EndX=7 EndY=1.8 EndZ=0
    g1: LineSegment StartX=0 StartY=-1.8 StartZ=0 EndX=7 EndY=-1.8 EndZ=0
    g2: ArcOfCircle CenterX=-5e-15 CenterY=1e-16 CenterZ=0 NormalX=0 NormalY=0 NormalZ=1 AngleXU=0 Radius=1.8 StartAngle=1.5708 EndAngle=4.71239
    g3: ArcOfCircle CenterX=7 CenterY=-1.05e-14 CenterZ=0 NormalX=0 NormalY=0 NormalZ=1 AngleXU=0 Radius=1.8 StartAngle=4.71239 EndAngle=7.85398
  constraints (9):
    c: PointOnObject(g0,g-2)
    c: Horizontal(g0)
    c: Tangent(g3,g1) = -1.5708
    c: Tangent(g3,g0) = 1.5708
    c: Tangent(g2,g1) = -1.5708
    c: Tangent(g2,g0) = 1.5708
    c: Symmetric(g1,g0,g-1)
    c: Radius(g2) = 1.8
    c: DistanceX(g2,g3) = 7
FEATURE [Part::Extrusion] Extrude006  label="screw hole sketch extrude"
  Base = -> Sketch008
  Dir = (0,0,1)
  DirMode = 2
  FaceMakerClass = Part::FaceMakerBullseye
  LengthFwd = 10
  LengthRev = 0
  Solid = true
  Symmetric = false
FEATURE [Part::Extrusion] Extrude007  label="screw top hole sketch extrude"
  Base = -> Sketch007
  Dir = (0,0,1)
  DirMode = 2
  FaceMakerClass = Part::FaceMakerBullseye
  LengthFwd = 10
  LengthRev = 0
  Reversed = true
  Solid = true
  Symmetric = false
FEATURE [Part::Loft] Loft
  Closed = false
  MaxDegree = 5
  Ruled = true
  Sections = -> [Sketch007,Sketch008]
  Solid = true
FEATURE [Part::MultiFuse] Fusion010  label="screw hole fusion"
  Placement = pos=(58,0,16) rot=(0,1,0;1.5708rad)
  Shapes = -> [Cylinder009,Extrude007,Extrude006,Loft]
FEATURE [Part::FeaturePython] Array006  label="screw hole array"  # Draft array (typed FeaturePython)
  AlwaysSyncPlacement = false
  Angle = 360
  ArrayType = 0
  Axis = (0,0,1)
  Base = -> Fusion010
  Center = (0,0,0)
  Count = 2
  ExpandArray = false
  Fuse = false
  IntervalAxis = (0,0,0)
  IntervalX = (100,0,0)
  IntervalY = (0,100,0)
  IntervalZ = (0,0,20)
  NumberCircles = 3
  NumberPolar = 5
  NumberX = 1
  NumberY = 1
  NumberZ = 2
  PlacementList = 2 placements: [(58,0,16),(58,0,36)]
  RadialDistance = 50
  ScaleList = (2) [(1,1,1),(1,1,1)]
  Symmetry = 1
  TangentialDistance = 25
FEATURE [Part::MultiFuse] Fusion009  label="hand hole fusion"
  Shapes = -> [Part__Mirroring,Cylinder007,Array006]
FEATURE [Part::Cut] Cut011  label="hand cut"
  Base = -> Fillet
  Tool = -> Fusion009
FEATURE [Part::Compound] Compound002  label="hand compound"
  Links = -> [Cut011]
  Placement = pos=(0,48.8,0) rot=(0,0,1;0rad)
